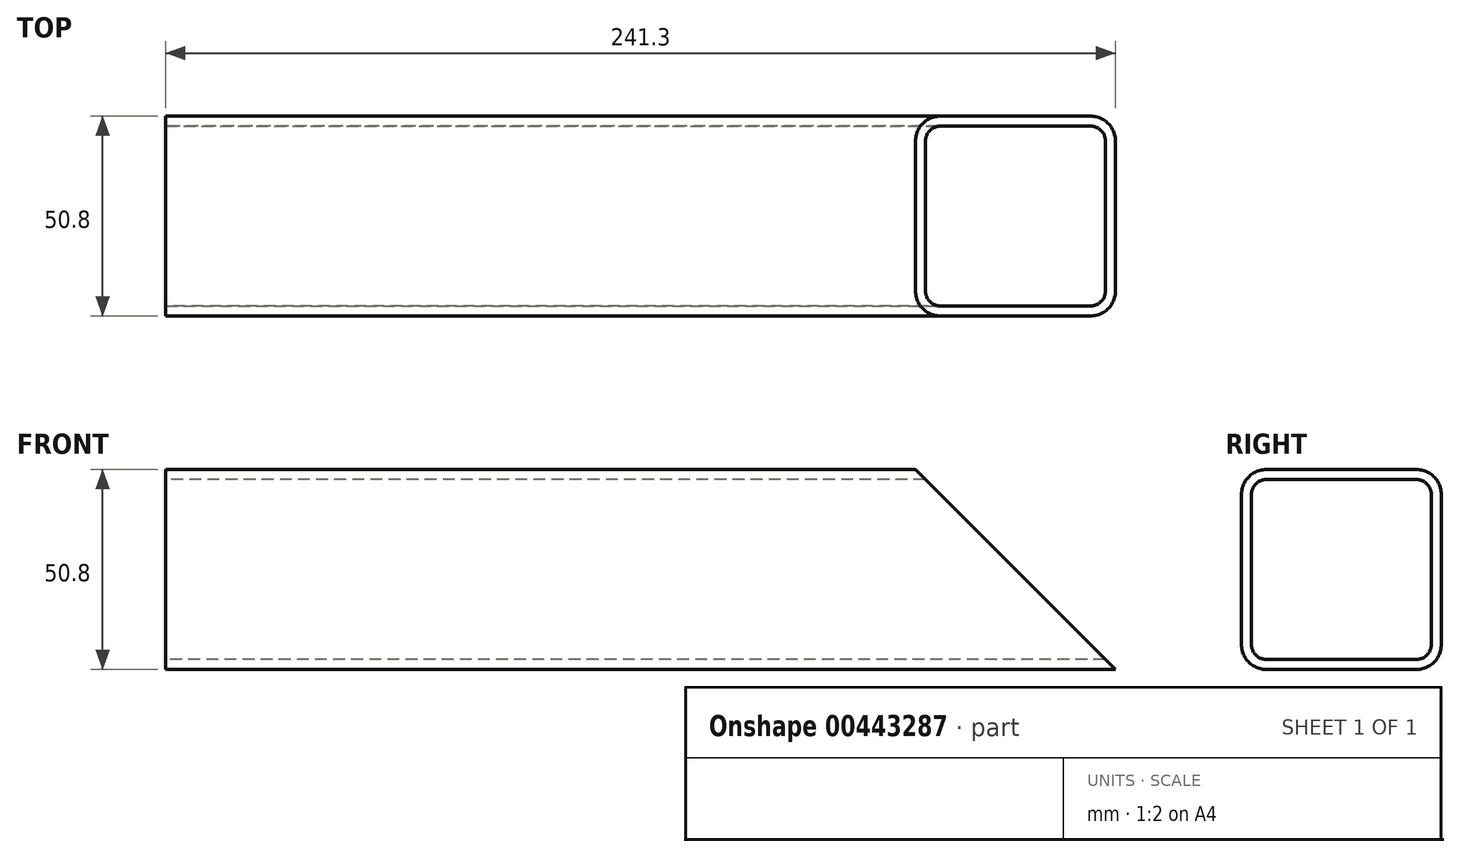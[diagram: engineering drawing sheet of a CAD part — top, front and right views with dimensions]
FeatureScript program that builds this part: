
annotation { "Feature Type Name" : "Feature", "Feature Type Description" : "" }
export const myFeature = defineFeature(function(context is Context, id is Id, definition is map)
    precondition{}
    {
        {
            var Q0;
            Q0=qCreatedBy(makeId("Right.planeOp"),FACE);
            var sketch = newSketch(context, id + "F0", { "sketchPlane" : qUnion([Q0])});
            skLineSegment(sketch, "E0.bottom", {"start": v(19.05, 25.4) * mm, "end": v(-19.05, 25.4) * mm});
            skLineSegment(sketch, "E0.top", {"start": v(19.05, -25.4) * mm, "end": v(-19.05, -25.4) * mm});
            skLineSegment(sketch, "E0.left", {"start": v(25.4, 19.05) * mm, "end": v(25.4, -19.05) * mm});
            skLineSegment(sketch, "E0.right", {"start": v(-25.4, 19.05) * mm, "end": v(-25.4, -19.05) * mm});
            skPoint(sketch, "E0.middle", {"position": v(0, 0) * mm});
            skPoint(sketch, "E1.visualSharp", {"position": v(-25.4, 25.4) * mm});
            skArc(sketch, "E1.filletArc", {"start": v(-19.05, 25.4) * mm, "mid": v(-23.54, 23.54) * mm, "end": v(-25.4, 19.05) * mm});
            skPoint(sketch, "E2.visualSharp", {"position": v(25.4, 25.4) * mm});
            skArc(sketch, "E2.filletArc", {"start": v(25.4, 19.05) * mm, "mid": v(23.54, 23.54) * mm, "end": v(19.05, 25.4) * mm});
            skPoint(sketch, "E3.visualSharp", {"position": v(25.4, -25.4) * mm});
            skArc(sketch, "E3.filletArc", {"start": v(19.05, -25.4) * mm, "mid": v(23.54, -23.54) * mm, "end": v(25.4, -19.05) * mm});
            skPoint(sketch, "E4.visualSharp", {"position": v(-25.4, -25.4) * mm});
            skArc(sketch, "E4.filletArc", {"start": v(-25.4, -19.05) * mm, "mid": v(-23.54, -23.54) * mm, "end": v(-19.05, -25.4) * mm});
            skSolve(sketch);
        }
        {
            var Q0;
            Q0 = qSketchRegion(id + "F0", true);
            extrude(context, id + "F1", {"entities" : qUnion([Q0]), "depth" : 254 * mm});
        }
        {
            var Q0;
            Q0=makeQuery(id+"F1.opExtrude","CAP_FACE",FACE,{"disambiguationData":[OSD([sQuery(id+"F0.wireOp",EDGE,"E0.bottom"),sQuery(id+"F0.wireOp",EDGE,"E0.top"),sQuery(id+"F0.wireOp",EDGE,"E0.left"),sQuery(id+"F0.wireOp",EDGE,"E0.right"),sQuery(id+"F0.wireOp",EDGE,"E1.filletArc"),sQuery(id+"F0.wireOp",EDGE,"E2.filletArc"),sQuery(id+"F0.wireOp",EDGE,"E3.filletArc"),sQuery(id+"F0.wireOp",EDGE,"E4.filletArc")])],"isStart":false});
            var Q1;
            Q1=makeQuery(id+"F1.opExtrude","CAP_FACE",FACE,{"disambiguationData":[OSD([sQuery(id+"F0.wireOp",EDGE,"E0.bottom"),sQuery(id+"F0.wireOp",EDGE,"E0.top"),sQuery(id+"F0.wireOp",EDGE,"E0.left"),sQuery(id+"F0.wireOp",EDGE,"E0.right"),sQuery(id+"F0.wireOp",EDGE,"E1.filletArc"),sQuery(id+"F0.wireOp",EDGE,"E2.filletArc"),sQuery(id+"F0.wireOp",EDGE,"E3.filletArc"),sQuery(id+"F0.wireOp",EDGE,"E4.filletArc")])],"isStart":true});
            shell(context, id + "F2", {"entities" : qUnion([Q0, Q1]), "thickness" : 2.54 * mm});
        }
        {
            var Q0;
            Q0=qCreatedBy(makeId("Front.planeOp"),FACE);
            var sketch = newSketch(context, id + "F3", { "sketchPlane" : qUnion([Q0])});
            skLineSegment(sketch, "E5", {"start": v(190.5, 25.4) * mm, "end": v(241.3, -25.4) * mm});
            skLineSegment(sketch, "E6", {"start": v(241.3, -25.4) * mm, "end": v(254, -25.4) * mm});
            skLineSegment(sketch, "E7", {"start": v(254, -25.4) * mm, "end": v(254, 25.4) * mm});
            skLineSegment(sketch, "E8", {"start": v(254, 25.4) * mm, "end": v(190.5, 25.4) * mm});
            skSolve(sketch);
        }
        {
            var Q0;
            Q0 = qSketchRegion(id + "F3", true);
            extrude(context, id + "F4", {"entities" : qUnion([Q0]), "operationType" : NewBodyOperationType.REMOVE, "endBound" : BoundingType.SYMMETRIC, "oppositeDirection" : true, "depth" : 50.8 * mm});
        }
    });
